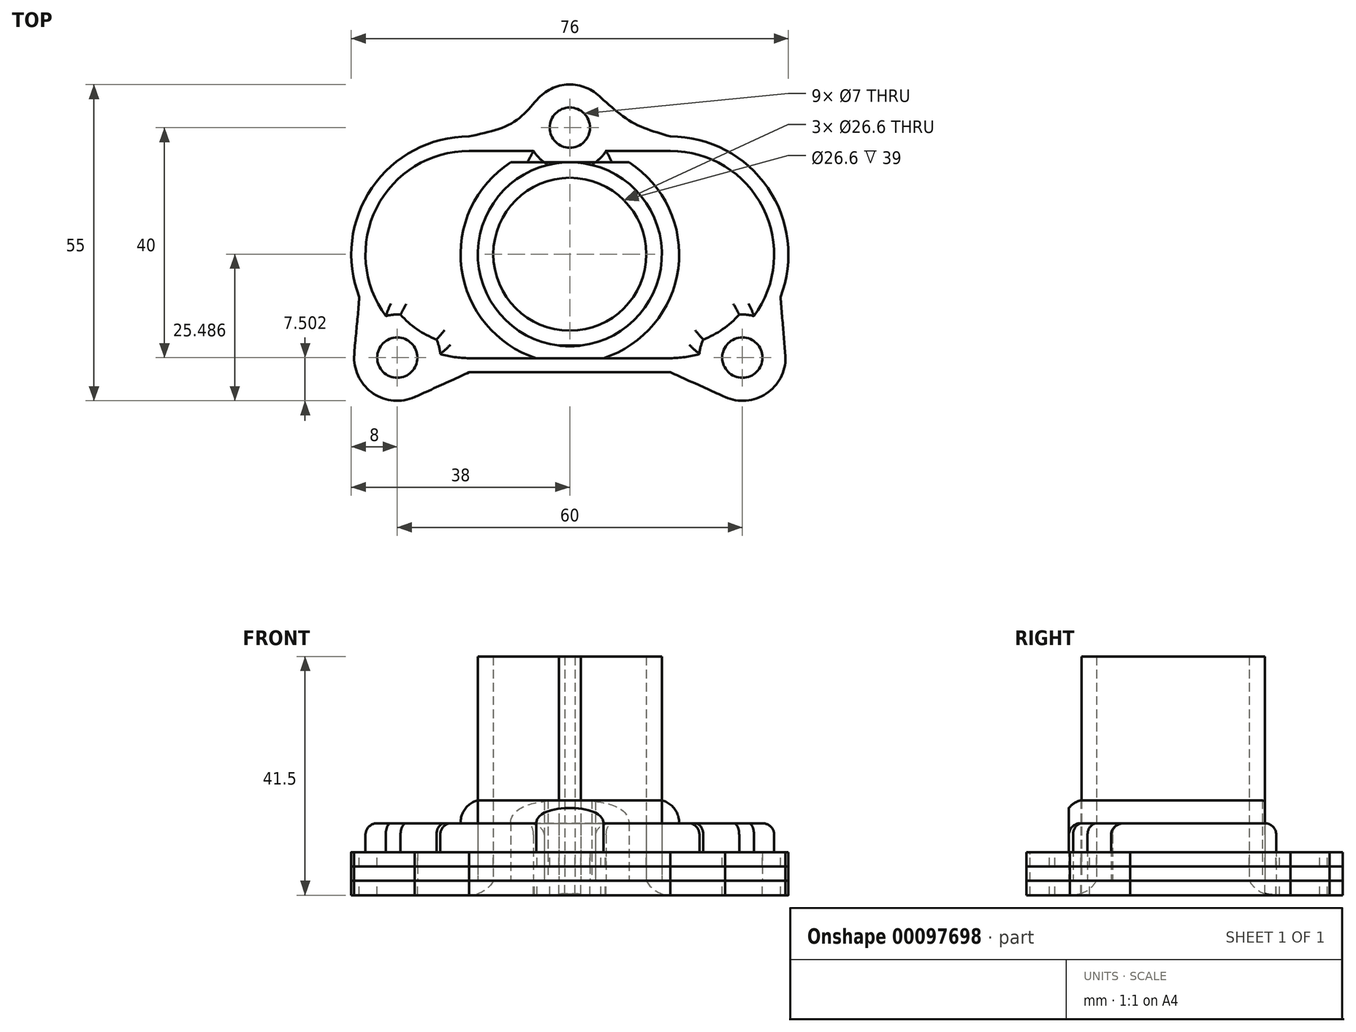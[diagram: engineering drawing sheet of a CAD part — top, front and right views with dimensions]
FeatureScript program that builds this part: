
annotation { "Feature Type Name" : "Feature", "Feature Type Description" : "" }
export const myFeature = defineFeature(function(context is Context, id is Id, definition is map)
    precondition{}
    {
        {
            var Q0;
            Q0=qCreatedBy(makeId("Top.planeOp"),FACE);
            var sketch = newSketch(context, id + "F0", { "sketchPlane" : qUnion([Q0])});
            skCircle(sketch, "E0", {"center": v(0, 24.43) * mm, "radius": 3.5 * mm});
            skCircle(sketch, "E1", {"center": v(30, -15.57) * mm, "radius": 3.5 * mm});
            skCircle(sketch, "E2", {"center": v(-30, -15.57) * mm, "radius": 3.5 * mm});
            skCircle(sketch, "E3", {"center": v(0, 24.43) * mm, "radius": 7.5 * mm});
            skCircle(sketch, "E4", {"center": v(30, -15.57) * mm, "radius": 7.5 * mm});
            skCircle(sketch, "E5", {"center": v(-30, -15.57) * mm, "radius": 7.5 * mm});
            skLineSegment(sketch, "E6", {"start": v(7.34, 22.9) * mm, "end": v(17.5, 22.9) * mm});
            skLineSegment(sketch, "E7", {"start": v(-17.5, -18.1) * mm, "end": v(17.5, -18.1) * mm});
            skLineSegment(sketch, "E8", {"start": v(-7.7, 22.9) * mm, "end": v(-17.5, 22.9) * mm});
            skLineSegment(sketch, "E9", {"start": v(-17.5, 15.9) * mm, "end": v(17.5, 15.9) * mm});
            skLineSegment(sketch, "E10", {"start": v(-17.5, -11.1) * mm, "end": v(17.5, -11.1) * mm});
            skArc(sketch, "E11", {"start": v(17.5, -11.1) * mm, "mid": v(31, 2.4) * mm, "end": v(17.5, 15.9) * mm});
            skArc(sketch, "E12", {"start": v(-17.5, 15.9) * mm, "mid": v(-31, 2.4) * mm, "end": v(-17.5, -11.1) * mm});
            skFitSpline(sketch, "E13", {"points": [v(-17.5, 22.9) * mm, v(-10.03, 25.23) * mm, v(-5.72, 29.28) * mm], "startDerivative": vector(15.12, 3.6) * mm, "endDerivative": vector(8.27, 9.34) * mm});
            skFitSpline(sketch, "E14", {"points": [v(17.5, 22.9) * mm, v(11.1, 25.23) * mm, v(5.4, 29.63) * mm], "startDerivative": vector(-13.33, 4.18) * mm, "endDerivative": vector(-10.87, 9.3) * mm});
            skArc(sketch, "E15", {"start": v(17.5, -18.1) * mm, "mid": v(38, 2.4) * mm, "end": v(17.5, 22.9) * mm});
            skArc(sketch, "E16", {"start": v(-17.5, 22.9) * mm, "mid": v(-38, 2.4) * mm, "end": v(-17.5, -18.1) * mm});
            skFitSpline(sketch, "E17", {"points": [v(27, -22.44) * mm, v(17.5, -18.1) * mm], "startDerivative": vector(-8.6, 4.02) * mm, "endDerivative": vector(-8.6, 4.02) * mm});
            skFitSpline(sketch, "E18", {"points": [v(-17.5, -18.1) * mm, v(-27, -22.44) * mm], "startDerivative": vector(-8, -3.6) * mm, "endDerivative": vector(-8, -3.6) * mm});
            skFitSpline(sketch, "E19", {"points": [v(36.62, -5) * mm, v(37.5, -15.5) * mm], "startDerivative": vector(0.87, -10.65) * mm, "endDerivative": vector(0.87, -10.65) * mm});
            skFitSpline(sketch, "E20", {"points": [v(-37.5, -15.5) * mm, v(-36.62, -5) * mm], "startDerivative": vector(0.62, 11.41) * mm, "endDerivative": vector(0.62, 11.41) * mm});
            skLineSegment(sketch, "E21", {"start": v(-17.5, 20.4) * mm, "end": v(17.5, 20.4) * mm});
            skLineSegment(sketch, "E22", {"start": v(-17.5, -15.66) * mm, "end": v(17.5, -15.66) * mm});
            skArc(sketch, "E23", {"start": v(17.5, -15.66) * mm, "mid": v(35.53, 2.36) * mm, "end": v(17.5, 20.4) * mm});
            skArc(sketch, "E24", {"start": v(-17.5, 20.4) * mm, "mid": v(-35.53, 2.36) * mm, "end": v(-17.5, -15.66) * mm});
            skLineSegment(sketch, "E25", {"start": v(-17.5, 18.4) * mm, "end": v(17.5, 18.4) * mm});
            skLineSegment(sketch, "E26", {"start": v(-17.5, -13.47) * mm, "end": v(17.5, -13.47) * mm});
            skArc(sketch, "E27", {"start": v(17.5, -13.47) * mm, "mid": v(33.43, 2.46) * mm, "end": v(17.5, 18.4) * mm});
            skArc(sketch, "E28", {"start": v(-17.5, 18.4) * mm, "mid": v(-33.43, 2.46) * mm, "end": v(-17.5, -13.47) * mm});
            skCircle(sketch, "E29", {"center": v(0, 2.42) * mm, "radius": 16 * mm});
            skCircle(sketch, "E30", {"center": v(0, 2.42) * mm, "radius": 13.3 * mm});
            skCircle(sketch, "E31", {"center": v(0, 2.42) * mm, "radius": 19 * mm});
            skSolve(sketch);
        }
        {
            var Q0;
            {var subQ1=sQuery(id+"F0.wireOp",EDGE,"E13");Q0=makeQuery(id+"F0.imprint","IMPRINT",FACE,{"disambiguationData":[TD([[makeQuery(id+"F0.imprint","IMPRINT",EDGE,{"derivedFrom":subQ1}),-1.0]])]});}
            var Q1;
            {var subQ0=sQuery(id+"F0.wireOp",EDGE,"E16");var subQ1=sQuery(id+"F0.wireOp",EDGE,"E2");var subQ2=makeQuery(id+"F0.imprint","INTERSECT",VERTEX,{"disambiguationData":[OD(0.0)],"derivedFrom":[subQ1,subQ0]});Q1=makeQuery(id+"F0.imprint","IMPRINT",FACE,{"disambiguationData":[TD([[makeQuery(id+"F0.imprint","IMPRINT",EDGE,{"disambiguationData":[TD([[subQ2,1.0]])],"derivedFrom":subQ1}),-1.0]])]});}
            var Q2;
            {var subQ6=sQuery(id+"F0.wireOp",EDGE,"E7");Q2=makeQuery(id+"F0.imprint","IMPRINT",FACE,{"disambiguationData":[TD([[makeQuery(id+"F0.imprint","IMPRINT",EDGE,{"derivedFrom":subQ6}),1.0]])]});}
            var Q3;
            {var subQ0=sQuery(id+"F0.wireOp",EDGE,"E18");var subQ1=sQuery(id+"F0.wireOp",EDGE,"E5");var subQ2=makeQuery(id+"F0.imprint","INTERSECT",VERTEX,{"disambiguationData":[OD(1.0)],"derivedFrom":[subQ1,subQ0]});Q3=makeQuery(id+"F0.imprint","IMPRINT",FACE,{"disambiguationData":[TD([[makeQuery(id+"F0.imprint","IMPRINT",EDGE,{"disambiguationData":[TD([[subQ2,-1.0]])],"derivedFrom":subQ1}),-1.0]])]});}
            var Q4;
            {var subQ6=sQuery(id+"F0.wireOp",EDGE,"E16");var subQ10=sQuery(id+"F0.wireOp",EDGE,"E2");var subQ11=makeQuery(id+"F0.imprint","INTERSECT",VERTEX,{"disambiguationData":[OD(0.0)],"derivedFrom":[subQ10,subQ6]});Q4=makeQuery(id+"F0.imprint","IMPRINT",FACE,{"disambiguationData":[TD([[makeQuery(id+"F0.imprint","IMPRINT",EDGE,{"disambiguationData":[TD([[subQ11,-1.0]])],"derivedFrom":subQ10}),-1.0]])]});}
            var Q5;
            {var subQ0=sQuery(id+"F0.wireOp",EDGE,"E20");var subQ1=sQuery(id+"F0.wireOp",EDGE,"E5");var subQ2=makeQuery(id+"F0.imprint","INTERSECT",VERTEX,{"disambiguationData":[OD(1.0)],"derivedFrom":[subQ1,subQ0]});Q5=makeQuery(id+"F0.imprint","IMPRINT",FACE,{"disambiguationData":[TD([[makeQuery(id+"F0.imprint","IMPRINT",EDGE,{"disambiguationData":[TD([[subQ2,1.0]])],"derivedFrom":subQ1}),-1.0]])]});}
            var Q6;
            {var subQ0=sQuery(id+"F0.wireOp",EDGE,"E6");Q6=makeQuery(id+"F0.imprint","IMPRINT",FACE,{"disambiguationData":[TD([[makeQuery(id+"F0.imprint","IMPRINT",EDGE,{"derivedFrom":subQ0}),1.0]])]});}
            var Q7;
            {var subQ0=sQuery(id+"F0.wireOp",EDGE,"E6");Q7=makeQuery(id+"F0.imprint","IMPRINT",FACE,{"disambiguationData":[TD([[makeQuery(id+"F0.imprint","IMPRINT",EDGE,{"derivedFrom":subQ0}),-1.0]])]});}
            var Q8;
            {var subQ0=sQuery(id+"F0.wireOp",EDGE,"E19");var subQ1=sQuery(id+"F0.wireOp",EDGE,"E4");var subQ2=makeQuery(id+"F0.imprint","INTERSECT",VERTEX,{"disambiguationData":[OD(1.0)],"derivedFrom":[subQ1,subQ0]});Q8=makeQuery(id+"F0.imprint","IMPRINT",FACE,{"disambiguationData":[TD([[makeQuery(id+"F0.imprint","IMPRINT",EDGE,{"disambiguationData":[TD([[subQ2,-1.0]])],"derivedFrom":subQ1}),-1.0]])]});}
            var Q9;
            {var subQ6=sQuery(id+"F0.wireOp",EDGE,"E15");var subQ10=sQuery(id+"F0.wireOp",EDGE,"E1");var subQ12=makeQuery(id+"F0.imprint","INTERSECT",VERTEX,{"disambiguationData":[OD(0.0)],"derivedFrom":[subQ10,subQ6]});Q9=makeQuery(id+"F0.imprint","IMPRINT",FACE,{"disambiguationData":[TD([[makeQuery(id+"F0.imprint","IMPRINT",EDGE,{"disambiguationData":[TD([[subQ12,-1.0]])],"derivedFrom":subQ10}),-1.0]])]});}
            var Q10;
            {var subQ0=sQuery(id+"F0.wireOp",EDGE,"E17");var subQ1=sQuery(id+"F0.wireOp",EDGE,"E4");var subQ2=makeQuery(id+"F0.imprint","INTERSECT",VERTEX,{"disambiguationData":[OD(1.0)],"derivedFrom":[subQ1,subQ0]});Q10=makeQuery(id+"F0.imprint","IMPRINT",FACE,{"disambiguationData":[TD([[makeQuery(id+"F0.imprint","IMPRINT",EDGE,{"disambiguationData":[TD([[subQ2,1.0]])],"derivedFrom":subQ1}),-1.0]])]});}
            var Q11;
            {var subQ0=sQuery(id+"F0.wireOp",EDGE,"E15");var subQ5=sQuery(id+"F0.wireOp",EDGE,"E1");var subQ6=makeQuery(id+"F0.imprint","INTERSECT",VERTEX,{"disambiguationData":[OD(0.0)],"derivedFrom":[subQ5,subQ0]});Q11=makeQuery(id+"F0.imprint","IMPRINT",FACE,{"disambiguationData":[TD([[makeQuery(id+"F0.imprint","IMPRINT",EDGE,{"disambiguationData":[TD([[subQ6,1.0]])],"derivedFrom":subQ5}),-1.0]])]});}
            var Q12;
            {var subQ0=sQuery(id+"F0.wireOp",EDGE,"E25");var subQ1=sQuery(id+"F0.wireOp",EDGE,"E3");var subQ2=makeQuery(id+"F0.imprint","INTERSECT",VERTEX,{"disambiguationData":[OD(0.0)],"derivedFrom":[subQ1,subQ0]});Q12=makeQuery(id+"F0.imprint","IMPRINT",FACE,{"disambiguationData":[TD([[makeQuery(id+"F0.imprint","IMPRINT",EDGE,{"disambiguationData":[TD([[subQ2,-1.0]])],"derivedFrom":subQ1}),1.0]])]});}
            var Q13;
            {var subQ0=sQuery(id+"F0.wireOp",EDGE,"E28");var subQ1=sQuery(id+"F0.wireOp",EDGE,"E5");var subQ2=makeQuery(id+"F0.imprint","INTERSECT",VERTEX,{"disambiguationData":[OD(0.0)],"derivedFrom":[subQ1,subQ0]});Q13=makeQuery(id+"F0.imprint","IMPRINT",FACE,{"disambiguationData":[TD([[makeQuery(id+"F0.imprint","IMPRINT",EDGE,{"disambiguationData":[TD([[subQ2,-1.0]])],"derivedFrom":subQ1}),1.0]])]});}
            var Q14;
            {var subQ0=sQuery(id+"F0.wireOp",EDGE,"E27");var subQ1=sQuery(id+"F0.wireOp",EDGE,"E4");var subQ2=makeQuery(id+"F0.imprint","INTERSECT",VERTEX,{"disambiguationData":[OD(0.0)],"derivedFrom":[subQ1,subQ0]});Q14=makeQuery(id+"F0.imprint","IMPRINT",FACE,{"disambiguationData":[TD([[makeQuery(id+"F0.imprint","IMPRINT",EDGE,{"disambiguationData":[TD([[subQ2,-1.0]])],"derivedFrom":subQ1}),1.0]])]});}
            var Q15;
            {var subQ0=sQuery(id+"F0.wireOp",EDGE,"E21");var subQ1=sQuery(id+"F0.wireOp",EDGE,"E3");var subQ2=makeQuery(id+"F0.imprint","INTERSECT",VERTEX,{"disambiguationData":[OD(0.0)],"derivedFrom":[subQ1,subQ0]});Q15=makeQuery(id+"F0.imprint","IMPRINT",FACE,{"disambiguationData":[TD([[makeQuery(id+"F0.imprint","IMPRINT",EDGE,{"disambiguationData":[TD([[subQ2,-1.0]])],"derivedFrom":subQ1}),1.0]])]});}
            var Q16;
            {var subQ0=sQuery(id+"F0.wireOp",EDGE,"E12");Q16=makeQuery(id+"F0.imprint","IMPRINT",FACE,{"disambiguationData":[TD([[makeQuery(id+"F0.imprint","IMPRINT",EDGE,{"derivedFrom":subQ0}),-1.0]])]});}
            var Q17;
            {var subQ0=sQuery(id+"F0.wireOp",EDGE,"E11");Q17=makeQuery(id+"F0.imprint","IMPRINT",FACE,{"disambiguationData":[TD([[makeQuery(id+"F0.imprint","IMPRINT",EDGE,{"derivedFrom":subQ0}),-1.0]])]});}
            var Q18;
            {var subQ0=sQuery(id+"F0.wireOp",EDGE,"E29");var subQ1=sQuery(id+"F0.wireOp",EDGE,"E3");var subQ2=makeQuery(id+"F0.imprint","INTERSECT",VERTEX,{"disambiguationData":[OD(0.0)],"derivedFrom":[subQ1,subQ0]});Q18=makeQuery(id+"F0.imprint","IMPRINT",FACE,{"disambiguationData":[TD([[makeQuery(id+"F0.imprint","IMPRINT",EDGE,{"disambiguationData":[TD([[subQ2,-1.0]])],"derivedFrom":subQ1}),-1.0]])]});}
            var Q19;
            {var subQ0=sQuery(id+"F0.wireOp",EDGE,"E29");var subQ1=sQuery(id+"F0.wireOp",EDGE,"E3");var subQ2=makeQuery(id+"F0.imprint","INTERSECT",VERTEX,{"disambiguationData":[OD(0.0)],"derivedFrom":[subQ1,subQ0]});Q19=makeQuery(id+"F0.imprint","IMPRINT",FACE,{"disambiguationData":[TD([[makeQuery(id+"F0.imprint","IMPRINT",EDGE,{"disambiguationData":[TD([[subQ2,-1.0]])],"derivedFrom":subQ1}),1.0]])]});}
            var Q20;
            {var subQ0=sQuery(id+"F0.wireOp",EDGE,"E29");var subQ1=sQuery(id+"F0.wireOp",EDGE,"E3");var subQ2=makeQuery(id+"F0.imprint","INTERSECT",VERTEX,{"disambiguationData":[OD(1.0)],"derivedFrom":[subQ1,subQ0]});Q20=makeQuery(id+"F0.imprint","IMPRINT",FACE,{"disambiguationData":[TD([[makeQuery(id+"F0.imprint","IMPRINT",EDGE,{"disambiguationData":[TD([[subQ2,-1.0]])],"derivedFrom":subQ1}),1.0]])]});}
            var Q21;
            {var subQ0=sQuery(id+"F0.wireOp",EDGE,"E11");Q21=makeQuery(id+"F0.imprint","IMPRINT",FACE,{"disambiguationData":[TD([[makeQuery(id+"F0.imprint","IMPRINT",EDGE,{"derivedFrom":subQ0}),1.0]])]});}
            var Q22;
            {var subQ0=sQuery(id+"F0.wireOp",EDGE,"E12");Q22=makeQuery(id+"F0.imprint","IMPRINT",FACE,{"disambiguationData":[TD([[makeQuery(id+"F0.imprint","IMPRINT",EDGE,{"derivedFrom":subQ0}),1.0]])]});}
            var Q23;
            Q23=makeQuery(id+"F0.imprint","IMPRINT",FACE,{"disambiguationData":[TD([[makeQuery(id+"F0.imprint","IMPRINT",EDGE,{"derivedFrom":sQuery(id+"F0.wireOp",EDGE,"E30")}),-1.0]])]});
            var Q24;
            {var subQ0=sQuery(id+"F0.wireOp",EDGE,"E29");var subQ1=sQuery(id+"F0.wireOp",EDGE,"E10");var subQ2=makeQuery(id+"F0.imprint","INTERSECT",VERTEX,{"disambiguationData":[OD(0.0)],"derivedFrom":[subQ1,subQ0]});Q24=makeQuery(id+"F0.imprint","IMPRINT",FACE,{"disambiguationData":[TD([[makeQuery(id+"F0.imprint","IMPRINT",EDGE,{"disambiguationData":[TD([[subQ2,-1.0]])],"derivedFrom":subQ1}),-1.0]])]});}
            var Q25;
            {var subQ0=sQuery(id+"F0.wireOp",EDGE,"E31");var subQ1=sQuery(id+"F0.wireOp",EDGE,"E22");var subQ2=makeQuery(id+"F0.imprint","INTERSECT",VERTEX,{"disambiguationData":[OD(0.0)],"derivedFrom":[subQ1,subQ0]});Q25=makeQuery(id+"F0.imprint","IMPRINT",FACE,{"disambiguationData":[TD([[makeQuery(id+"F0.imprint","IMPRINT",EDGE,{"disambiguationData":[TD([[subQ2,-1.0]])],"derivedFrom":subQ1}),-1.0]])]});}
            var Q26;
            {var subQ0=sQuery(id+"F0.wireOp",EDGE,"E29");var subQ1=sQuery(id+"F0.wireOp",EDGE,"E9");var subQ2=makeQuery(id+"F0.imprint","INTERSECT",VERTEX,{"disambiguationData":[OD(1.0)],"derivedFrom":[subQ1,subQ0]});Q26=makeQuery(id+"F0.imprint","IMPRINT",FACE,{"disambiguationData":[TD([[makeQuery(id+"F0.imprint","IMPRINT",EDGE,{"disambiguationData":[TD([[subQ2,-1.0]])],"derivedFrom":subQ1}),-1.0]])]});}
            var Q27;
            {var subQ0=sQuery(id+"F0.wireOp",EDGE,"E31");var subQ1=sQuery(id+"F0.wireOp",EDGE,"E9");var subQ2=makeQuery(id+"F0.imprint","INTERSECT",VERTEX,{"disambiguationData":[OD(0.0)],"derivedFrom":[subQ1,subQ0]});Q27=makeQuery(id+"F0.imprint","IMPRINT",FACE,{"disambiguationData":[TD([[makeQuery(id+"F0.imprint","IMPRINT",EDGE,{"disambiguationData":[TD([[subQ2,-1.0]])],"derivedFrom":subQ1}),-1.0]])]});}
            var Q28;
            {var subQ0=sQuery(id+"F0.wireOp",EDGE,"E31");var subQ1=sQuery(id+"F0.wireOp",EDGE,"E10");var subQ2=makeQuery(id+"F0.imprint","INTERSECT",VERTEX,{"disambiguationData":[OD(0.0)],"derivedFrom":[subQ1,subQ0]});Q28=makeQuery(id+"F0.imprint","IMPRINT",FACE,{"disambiguationData":[TD([[makeQuery(id+"F0.imprint","IMPRINT",EDGE,{"disambiguationData":[TD([[subQ2,-1.0]])],"derivedFrom":subQ1}),-1.0]])]});}
            var Q29;
            {var subQ0=sQuery(id+"F0.wireOp",EDGE,"E29");var subQ1=sQuery(id+"F0.wireOp",EDGE,"E10");var subQ2=makeQuery(id+"F0.imprint","INTERSECT",VERTEX,{"disambiguationData":[OD(1.0)],"derivedFrom":[subQ1,subQ0]});Q29=makeQuery(id+"F0.imprint","IMPRINT",FACE,{"disambiguationData":[TD([[makeQuery(id+"F0.imprint","IMPRINT",EDGE,{"disambiguationData":[TD([[subQ2,-1.0]])],"derivedFrom":subQ1}),-1.0]])]});}
            var Q30;
            {var subQ1=sQuery(id+"F0.wireOp",EDGE,"E3");var subQ7=sQuery(id+"F0.wireOp",EDGE,"E25");var subQ8=makeQuery(id+"F0.imprint","INTERSECT",VERTEX,{"disambiguationData":[OD(0.0)],"derivedFrom":[subQ1,subQ7]});Q30=makeQuery(id+"F0.imprint","IMPRINT",FACE,{"disambiguationData":[TD([[makeQuery(id+"F0.imprint","IMPRINT",EDGE,{"disambiguationData":[TD([[subQ8,-1.0]])],"derivedFrom":subQ1}),-1.0]])]});}
            var Q31;
            {var subQ1=sQuery(id+"F0.wireOp",EDGE,"E3");var subQ5=sQuery(id+"F0.wireOp",EDGE,"E29");var subQ6=makeQuery(id+"F0.imprint","INTERSECT",VERTEX,{"disambiguationData":[OD(1.0)],"derivedFrom":[subQ1,subQ5]});Q31=makeQuery(id+"F0.imprint","IMPRINT",FACE,{"disambiguationData":[TD([[makeQuery(id+"F0.imprint","IMPRINT",EDGE,{"disambiguationData":[TD([[subQ6,-1.0]])],"derivedFrom":subQ1}),-1.0]])]});}
            var Q32;
            {var subQ7=sQuery(id+"F0.wireOp",EDGE,"E31");var subQ8=sQuery(id+"F0.wireOp",EDGE,"E0");var subQ9=makeQuery(id+"F0.imprint","INTERSECT",VERTEX,{"disambiguationData":[OD(0.0)],"derivedFrom":[subQ8,subQ7]});Q32=makeQuery(id+"F0.imprint","IMPRINT",FACE,{"disambiguationData":[TD([[makeQuery(id+"F0.imprint","IMPRINT",EDGE,{"disambiguationData":[TD([[subQ9,-1.0]])],"derivedFrom":subQ8}),-1.0]])]});}
            var Q33;
            {var subQ0=sQuery(id+"F0.wireOp",EDGE,"E31");var subQ1=sQuery(id+"F0.wireOp",EDGE,"E0");var subQ2=makeQuery(id+"F0.imprint","INTERSECT",VERTEX,{"disambiguationData":[OD(0.0)],"derivedFrom":[subQ1,subQ0]});Q33=makeQuery(id+"F0.imprint","IMPRINT",FACE,{"disambiguationData":[TD([[makeQuery(id+"F0.imprint","IMPRINT",EDGE,{"disambiguationData":[TD([[subQ2,1.0]])],"derivedFrom":subQ1}),-1.0]])]});}
            var Q34;
            {var subQ0=sQuery(id+"F0.wireOp",EDGE,"E29");var subQ1=sQuery(id+"F0.wireOp",EDGE,"E26");var subQ2=makeQuery(id+"F0.imprint","INTERSECT",VERTEX,{"disambiguationData":[OD(0.0)],"derivedFrom":[subQ1,subQ0]});Q34=makeQuery(id+"F0.imprint","IMPRINT",FACE,{"disambiguationData":[TD([[makeQuery(id+"F0.imprint","IMPRINT",EDGE,{"disambiguationData":[TD([[subQ2,-1.0]])],"derivedFrom":subQ1}),-1.0]])]});}
            var Q35;
            {var subQ3=sQuery(id+"F0.wireOp",EDGE,"E5");var subQ5=sQuery(id+"F0.wireOp",EDGE,"E28");var subQ11=makeQuery(id+"F0.imprint","INTERSECT",VERTEX,{"disambiguationData":[OD(0.0)],"derivedFrom":[subQ3,subQ5]});Q35=makeQuery(id+"F0.imprint","IMPRINT",FACE,{"disambiguationData":[TD([[makeQuery(id+"F0.imprint","IMPRINT",EDGE,{"disambiguationData":[TD([[subQ11,1.0]])],"derivedFrom":subQ3}),-1.0]])]});}
            var Q36;
            {var subQ4=sQuery(id+"F0.wireOp",EDGE,"E31");var subQ7=sQuery(id+"F0.wireOp",EDGE,"E22");var subQ9=makeQuery(id+"F0.imprint","INTERSECT",VERTEX,{"disambiguationData":[OD(0.0)],"derivedFrom":[subQ7,subQ4]});Q36=makeQuery(id+"F0.imprint","IMPRINT",FACE,{"disambiguationData":[TD([[makeQuery(id+"F0.imprint","IMPRINT",EDGE,{"disambiguationData":[TD([[subQ9,-1.0]])],"derivedFrom":subQ7}),1.0]])]});}
            var Q37;
            {var subQ0=sQuery(id+"F0.wireOp",EDGE,"E27");var subQ9=sQuery(id+"F0.wireOp",EDGE,"E4");var subQ11=makeQuery(id+"F0.imprint","INTERSECT",VERTEX,{"disambiguationData":[OD(1.0)],"derivedFrom":[subQ9,subQ0]});Q37=makeQuery(id+"F0.imprint","IMPRINT",FACE,{"disambiguationData":[TD([[makeQuery(id+"F0.imprint","IMPRINT",EDGE,{"disambiguationData":[TD([[subQ11,-1.0]])],"derivedFrom":subQ9}),-1.0]])]});}
            var Q38;
            {var subQ0=sQuery(id+"F0.wireOp",EDGE,"E23");var subQ1=sQuery(id+"F0.wireOp",EDGE,"E4");var subQ2=makeQuery(id+"F0.imprint","INTERSECT",VERTEX,{"disambiguationData":[OD(0.0)],"derivedFrom":[subQ1,subQ0]});Q38=makeQuery(id+"F0.imprint","IMPRINT",FACE,{"disambiguationData":[TD([[makeQuery(id+"F0.imprint","IMPRINT",EDGE,{"disambiguationData":[TD([[subQ2,-1.0]])],"derivedFrom":subQ1}),1.0]])]});}
            var Q39;
            {var subQ7=sQuery(id+"F0.wireOp",EDGE,"E3");var subQ9=sQuery(id+"F0.wireOp",EDGE,"E31");var subQ10=makeQuery(id+"F0.imprint","INTERSECT",VERTEX,{"disambiguationData":[OD(1.0)],"derivedFrom":[subQ7,subQ9]});Q39=makeQuery(id+"F0.imprint","IMPRINT",FACE,{"disambiguationData":[TD([[makeQuery(id+"F0.imprint","IMPRINT",EDGE,{"disambiguationData":[TD([[subQ10,-1.0]])],"derivedFrom":subQ7}),-1.0]])]});}
            var Q40;
            {var subQ0=sQuery(id+"F0.wireOp",EDGE,"E28");var subQ1=sQuery(id+"F0.wireOp",EDGE,"E5");var subQ2=makeQuery(id+"F0.imprint","INTERSECT",VERTEX,{"disambiguationData":[OD(0.0)],"derivedFrom":[subQ1,subQ0]});Q40=makeQuery(id+"F0.imprint","IMPRINT",FACE,{"disambiguationData":[TD([[makeQuery(id+"F0.imprint","IMPRINT",EDGE,{"disambiguationData":[TD([[subQ2,1.0]])],"derivedFrom":subQ1}),1.0]])]});}
            var Q41;
            {var subQ1=sQuery(id+"F0.wireOp",EDGE,"E21");var subQ5=sQuery(id+"F0.wireOp",EDGE,"E3");var subQ6=makeQuery(id+"F0.imprint","INTERSECT",VERTEX,{"disambiguationData":[OD(0.0)],"derivedFrom":[subQ5,subQ1]});Q41=makeQuery(id+"F0.imprint","IMPRINT",FACE,{"disambiguationData":[TD([[makeQuery(id+"F0.imprint","IMPRINT",EDGE,{"disambiguationData":[TD([[subQ6,-1.0]])],"derivedFrom":subQ5}),-1.0]])]});}
            var Q42;
            {var subQ0=sQuery(id+"F0.wireOp",EDGE,"E31");var subQ1=sQuery(id+"F0.wireOp",EDGE,"E3");var subQ2=makeQuery(id+"F0.imprint","INTERSECT",VERTEX,{"disambiguationData":[OD(0.0)],"derivedFrom":[subQ1,subQ0]});Q42=makeQuery(id+"F0.imprint","IMPRINT",FACE,{"disambiguationData":[TD([[makeQuery(id+"F0.imprint","IMPRINT",EDGE,{"disambiguationData":[TD([[subQ2,-1.0]])],"derivedFrom":subQ1}),-1.0]])]});}
            var Q43;
            {var subQ1=sQuery(id+"F0.wireOp",EDGE,"E3");var subQ6=sQuery(id+"F0.wireOp",EDGE,"E31");var subQ12=makeQuery(id+"F0.imprint","INTERSECT",VERTEX,{"disambiguationData":[OD(0.0)],"derivedFrom":[subQ1,subQ6]});Q43=makeQuery(id+"F0.imprint","IMPRINT",FACE,{"disambiguationData":[TD([[makeQuery(id+"F0.imprint","IMPRINT",EDGE,{"disambiguationData":[TD([[subQ12,-1.0]])],"derivedFrom":subQ1}),1.0]])]});}
            var Q44;
            {var subQ0=sQuery(id+"F0.wireOp",EDGE,"E25");var subQ1=sQuery(id+"F0.wireOp",EDGE,"E3");var subQ2=makeQuery(id+"F0.imprint","INTERSECT",VERTEX,{"disambiguationData":[OD(1.0)],"derivedFrom":[subQ1,subQ0]});Q44=makeQuery(id+"F0.imprint","IMPRINT",FACE,{"disambiguationData":[TD([[makeQuery(id+"F0.imprint","IMPRINT",EDGE,{"disambiguationData":[TD([[subQ2,-1.0]])],"derivedFrom":subQ1}),-1.0]])]});}
            var Q45;
            {var subQ0=sQuery(id+"F0.wireOp",EDGE,"E29");var subQ1=sQuery(id+"F0.wireOp",EDGE,"E25");var subQ2=makeQuery(id+"F0.imprint","INTERSECT",VERTEX,{"disambiguationData":[OD(0.0)],"derivedFrom":[subQ1,subQ0]});Q45=makeQuery(id+"F0.imprint","IMPRINT",FACE,{"disambiguationData":[TD([[makeQuery(id+"F0.imprint","IMPRINT",EDGE,{"disambiguationData":[TD([[subQ2,-1.0]])],"derivedFrom":subQ1}),1.0]])]});}
            extrude(context, id + "F1", {"entities" : qUnion([Q0, Q1, Q2, Q3, Q4, Q5, Q6, Q7, Q8, Q9, Q10, Q11, Q12, Q13, Q14, Q15, Q16, Q17, Q18, Q19, Q20, Q21, Q22, Q23, Q24, Q25, Q26, Q27, Q28, Q29, Q30, Q31, Q32, Q33, Q34, Q35, Q36, Q37, Q38, Q39, Q40, Q41, Q42, Q43, Q44, Q45]), "depth" : 5 * mm});
        }
        {
            var Q0;
            {var subQ0=sQuery(id+"F0.wireOp",EDGE,"E18");var subQ1=sQuery(id+"F0.wireOp",EDGE,"E5");var subQ2=makeQuery(id+"F0.imprint","INTERSECT",VERTEX,{"disambiguationData":[OD(1.0)],"derivedFrom":[subQ1,subQ0]});Q0=makeQuery(id+"F0.imprint","IMPRINT",FACE,{"disambiguationData":[TD([[makeQuery(id+"F0.imprint","IMPRINT",EDGE,{"disambiguationData":[TD([[subQ2,-1.0]])],"derivedFrom":subQ1}),-1.0]])]});}
            var Q1;
            {var subQ3=sQuery(id+"F0.wireOp",EDGE,"E16");var subQ5=sQuery(id+"F0.wireOp",EDGE,"E2");var subQ6=makeQuery(id+"F0.imprint","INTERSECT",VERTEX,{"disambiguationData":[OD(0.0)],"derivedFrom":[subQ5,subQ3]});Q1=makeQuery(id+"F0.imprint","IMPRINT",FACE,{"disambiguationData":[TD([[makeQuery(id+"F0.imprint","IMPRINT",EDGE,{"disambiguationData":[TD([[subQ6,-1.0]])],"derivedFrom":subQ5}),-1.0]])]});}
            var Q2;
            {var subQ0=sQuery(id+"F0.wireOp",EDGE,"E16");var subQ1=sQuery(id+"F0.wireOp",EDGE,"E2");var subQ2=makeQuery(id+"F0.imprint","INTERSECT",VERTEX,{"disambiguationData":[OD(0.0)],"derivedFrom":[subQ1,subQ0]});Q2=makeQuery(id+"F0.imprint","IMPRINT",FACE,{"disambiguationData":[TD([[makeQuery(id+"F0.imprint","IMPRINT",EDGE,{"disambiguationData":[TD([[subQ2,1.0]])],"derivedFrom":subQ1}),-1.0]])]});}
            var Q3;
            {var subQ1=sQuery(id+"F0.wireOp",EDGE,"E7");Q3=makeQuery(id+"F0.imprint","IMPRINT",FACE,{"disambiguationData":[TD([[makeQuery(id+"F0.imprint","IMPRINT",EDGE,{"derivedFrom":subQ1}),1.0]])]});}
            var Q4;
            {var subQ0=sQuery(id+"F0.wireOp",EDGE,"E25");var subQ1=sQuery(id+"F0.wireOp",EDGE,"E3");var subQ2=makeQuery(id+"F0.imprint","INTERSECT",VERTEX,{"disambiguationData":[OD(0.0)],"derivedFrom":[subQ1,subQ0]});Q4=makeQuery(id+"F0.imprint","IMPRINT",FACE,{"disambiguationData":[TD([[makeQuery(id+"F0.imprint","IMPRINT",EDGE,{"disambiguationData":[TD([[subQ2,-1.0]])],"derivedFrom":subQ1}),1.0]])]});}
            var Q5;
            {var subQ0=sQuery(id+"F0.wireOp",EDGE,"E28");var subQ1=sQuery(id+"F0.wireOp",EDGE,"E5");var subQ2=makeQuery(id+"F0.imprint","INTERSECT",VERTEX,{"disambiguationData":[OD(0.0)],"derivedFrom":[subQ1,subQ0]});Q5=makeQuery(id+"F0.imprint","IMPRINT",FACE,{"disambiguationData":[TD([[makeQuery(id+"F0.imprint","IMPRINT",EDGE,{"disambiguationData":[TD([[subQ2,-1.0]])],"derivedFrom":subQ1}),1.0]])]});}
            var Q6;
            Q6=makeQuery(id+"F0.imprint","IMPRINT",FACE,{"disambiguationData":[TD([[makeQuery(id+"F0.imprint","IMPRINT",EDGE,{"derivedFrom":sQuery(id+"F0.wireOp",EDGE,"E9")}),1.0]])]});
            var Q7;
            {var subQ0=sQuery(id+"F0.wireOp",EDGE,"E27");var subQ1=sQuery(id+"F0.wireOp",EDGE,"E4");var subQ2=makeQuery(id+"F0.imprint","INTERSECT",VERTEX,{"disambiguationData":[OD(0.0)],"derivedFrom":[subQ1,subQ0]});Q7=makeQuery(id+"F0.imprint","IMPRINT",FACE,{"disambiguationData":[TD([[makeQuery(id+"F0.imprint","IMPRINT",EDGE,{"disambiguationData":[TD([[subQ2,-1.0]])],"derivedFrom":subQ1}),1.0]])]});}
            var Q8;
            {var subQ0=sQuery(id+"F0.wireOp",EDGE,"E6");Q8=makeQuery(id+"F0.imprint","IMPRINT",FACE,{"disambiguationData":[TD([[makeQuery(id+"F0.imprint","IMPRINT",EDGE,{"derivedFrom":subQ0}),-1.0]])]});}
            var Q9;
            Q9=makeQuery(id+"F0.imprint","IMPRINT",FACE,{"disambiguationData":[TD([[makeQuery(id+"F0.imprint","IMPRINT",EDGE,{"derivedFrom":sQuery(id+"F0.wireOp",EDGE,"E0")}),-1.0]])]});
            var Q10;
            {var subQ0=sQuery(id+"F0.wireOp",EDGE,"E6");Q10=makeQuery(id+"F0.imprint","IMPRINT",FACE,{"disambiguationData":[TD([[makeQuery(id+"F0.imprint","IMPRINT",EDGE,{"derivedFrom":subQ0}),1.0]])]});}
            var Q11;
            {var subQ1=sQuery(id+"F0.wireOp",EDGE,"E13");Q11=makeQuery(id+"F0.imprint","IMPRINT",FACE,{"disambiguationData":[TD([[makeQuery(id+"F0.imprint","IMPRINT",EDGE,{"derivedFrom":subQ1}),-1.0]])]});}
            var Q12;
            {var subQ0=sQuery(id+"F0.wireOp",EDGE,"E15");var subQ1=sQuery(id+"F0.wireOp",EDGE,"E1");var subQ2=makeQuery(id+"F0.imprint","INTERSECT",VERTEX,{"disambiguationData":[OD(0.0)],"derivedFrom":[subQ1,subQ0]});Q12=makeQuery(id+"F0.imprint","IMPRINT",FACE,{"disambiguationData":[TD([[makeQuery(id+"F0.imprint","IMPRINT",EDGE,{"disambiguationData":[TD([[subQ2,1.0]])],"derivedFrom":subQ1}),-1.0]])]});}
            var Q13;
            {var subQ6=sQuery(id+"F0.wireOp",EDGE,"E15");var subQ10=sQuery(id+"F0.wireOp",EDGE,"E1");var subQ11=makeQuery(id+"F0.imprint","INTERSECT",VERTEX,{"disambiguationData":[OD(0.0)],"derivedFrom":[subQ10,subQ6]});Q13=makeQuery(id+"F0.imprint","IMPRINT",FACE,{"disambiguationData":[TD([[makeQuery(id+"F0.imprint","IMPRINT",EDGE,{"disambiguationData":[TD([[subQ11,-1.0]])],"derivedFrom":subQ10}),-1.0]])]});}
            var Q14;
            {var subQ0=sQuery(id+"F0.wireOp",EDGE,"E19");var subQ1=sQuery(id+"F0.wireOp",EDGE,"E4");var subQ2=makeQuery(id+"F0.imprint","INTERSECT",VERTEX,{"disambiguationData":[OD(1.0)],"derivedFrom":[subQ1,subQ0]});Q14=makeQuery(id+"F0.imprint","IMPRINT",FACE,{"disambiguationData":[TD([[makeQuery(id+"F0.imprint","IMPRINT",EDGE,{"disambiguationData":[TD([[subQ2,-1.0]])],"derivedFrom":subQ1}),-1.0]])]});}
            var Q15;
            {var subQ0=sQuery(id+"F0.wireOp",EDGE,"E17");var subQ1=sQuery(id+"F0.wireOp",EDGE,"E4");var subQ2=makeQuery(id+"F0.imprint","INTERSECT",VERTEX,{"disambiguationData":[OD(1.0)],"derivedFrom":[subQ1,subQ0]});Q15=makeQuery(id+"F0.imprint","IMPRINT",FACE,{"disambiguationData":[TD([[makeQuery(id+"F0.imprint","IMPRINT",EDGE,{"disambiguationData":[TD([[subQ2,1.0]])],"derivedFrom":subQ1}),-1.0]])]});}
            var Q16;
            {var subQ0=sQuery(id+"F0.wireOp",EDGE,"E20");var subQ1=sQuery(id+"F0.wireOp",EDGE,"E5");var subQ2=makeQuery(id+"F0.imprint","INTERSECT",VERTEX,{"disambiguationData":[OD(1.0)],"derivedFrom":[subQ1,subQ0]});Q16=makeQuery(id+"F0.imprint","IMPRINT",FACE,{"disambiguationData":[TD([[makeQuery(id+"F0.imprint","IMPRINT",EDGE,{"disambiguationData":[TD([[subQ2,1.0]])],"derivedFrom":subQ1}),-1.0]])]});}
            var Q17;
            {var subQ0=sQuery(id+"F0.wireOp",EDGE,"E29");var subQ1=sQuery(id+"F0.wireOp",EDGE,"E10");var subQ2=makeQuery(id+"F0.imprint","INTERSECT",VERTEX,{"disambiguationData":[OD(0.0)],"derivedFrom":[subQ1,subQ0]});Q17=makeQuery(id+"F0.imprint","IMPRINT",FACE,{"disambiguationData":[TD([[makeQuery(id+"F0.imprint","IMPRINT",EDGE,{"disambiguationData":[TD([[subQ2,-1.0]])],"derivedFrom":subQ1}),-1.0]])]});}
            var Q18;
            {var subQ15=sQuery(id+"F0.wireOp",EDGE,"E12");Q18=makeQuery(id+"F0.imprint","IMPRINT",FACE,{"disambiguationData":[TD([[makeQuery(id+"F0.imprint","IMPRINT",EDGE,{"derivedFrom":subQ15}),-1.0]])]});}
            var Q19;
            {var subQ0=sQuery(id+"F0.wireOp",EDGE,"E29");var subQ1=sQuery(id+"F0.wireOp",EDGE,"E3");var subQ2=makeQuery(id+"F0.imprint","INTERSECT",VERTEX,{"disambiguationData":[OD(0.0)],"derivedFrom":[subQ1,subQ0]});Q19=makeQuery(id+"F0.imprint","IMPRINT",FACE,{"disambiguationData":[TD([[makeQuery(id+"F0.imprint","IMPRINT",EDGE,{"disambiguationData":[TD([[subQ2,-1.0]])],"derivedFrom":subQ1}),1.0]])]});}
            var Q20;
            Q20=makeQuery(id+"F1.opExtrude","CAP_FACE",FACE,{"disambiguationData":[OSD([sQuery(id+"F0.wireOp",EDGE,"E0"),sQuery(id+"F0.wireOp",EDGE,"E1"),sQuery(id+"F0.wireOp",EDGE,"E2"),sQuery(id+"F0.wireOp",EDGE,"E3"),sQuery(id+"F0.wireOp",EDGE,"E4"),sQuery(id+"F0.wireOp",EDGE,"E5"),sQuery(id+"F0.wireOp",EDGE,"E7"),sQuery(id+"F0.wireOp",EDGE,"E13"),sQuery(id+"F0.wireOp",EDGE,"E14"),sQuery(id+"F0.wireOp",EDGE,"E15"),sQuery(id+"F0.wireOp",EDGE,"E16"),sQuery(id+"F0.wireOp",EDGE,"E17"),sQuery(id+"F0.wireOp",EDGE,"E18"),sQuery(id+"F0.wireOp",EDGE,"E19"),sQuery(id+"F0.wireOp",EDGE,"E20"),sQuery(id+"F0.wireOp",EDGE,"E25"),sQuery(id+"F0.wireOp",EDGE,"E26"),sQuery(id+"F0.wireOp",EDGE,"E27"),sQuery(id+"F0.wireOp",EDGE,"E28"),sQuery(id+"F0.wireOp",EDGE,"E29")])],"isStart":false});
            var Q21;
            {var subQ11=sQuery(id+"F0.wireOp",EDGE,"E11");Q21=makeQuery(id+"F0.imprint","IMPRINT",FACE,{"disambiguationData":[TD([[makeQuery(id+"F0.imprint","IMPRINT",EDGE,{"derivedFrom":subQ11}),-1.0]])]});}
            var Q22;
            {var subQ0=sQuery(id+"F0.wireOp",EDGE,"E12");Q22=makeQuery(id+"F0.imprint","IMPRINT",FACE,{"disambiguationData":[TD([[makeQuery(id+"F0.imprint","IMPRINT",EDGE,{"derivedFrom":subQ0}),1.0]])]});}
            var Q23;
            Q23=makeQuery(id+"F0.imprint","IMPRINT",FACE,{"disambiguationData":[TD([[makeQuery(id+"F0.imprint","IMPRINT",EDGE,{"derivedFrom":sQuery(id+"F0.wireOp",EDGE,"E30")}),-1.0]])]});
            var Q24;
            {var subQ0=sQuery(id+"F0.wireOp",EDGE,"E11");Q24=makeQuery(id+"F0.imprint","IMPRINT",FACE,{"disambiguationData":[TD([[makeQuery(id+"F0.imprint","IMPRINT",EDGE,{"derivedFrom":subQ0}),1.0]])]});}
            var Q25;
            {var subQ0=sQuery(id+"F0.wireOp",EDGE,"E31");var subQ1=sQuery(id+"F0.wireOp",EDGE,"E9");var subQ2=makeQuery(id+"F0.imprint","INTERSECT",VERTEX,{"disambiguationData":[OD(0.0)],"derivedFrom":[subQ1,subQ0]});Q25=makeQuery(id+"F0.imprint","IMPRINT",FACE,{"disambiguationData":[TD([[makeQuery(id+"F0.imprint","IMPRINT",EDGE,{"disambiguationData":[TD([[subQ2,-1.0]])],"derivedFrom":subQ1}),-1.0]])]});}
            var Q26;
            {var subQ1=sQuery(id+"F0.wireOp",EDGE,"E3");var subQ7=sQuery(id+"F0.wireOp",EDGE,"E25");var subQ8=makeQuery(id+"F0.imprint","INTERSECT",VERTEX,{"disambiguationData":[OD(0.0)],"derivedFrom":[subQ1,subQ7]});Q26=makeQuery(id+"F0.imprint","IMPRINT",FACE,{"disambiguationData":[TD([[makeQuery(id+"F0.imprint","IMPRINT",EDGE,{"disambiguationData":[TD([[subQ8,-1.0]])],"derivedFrom":subQ1}),-1.0]])]});}
            var Q27;
            {var subQ1=sQuery(id+"F0.wireOp",EDGE,"E3");var subQ5=sQuery(id+"F0.wireOp",EDGE,"E29");var subQ6=makeQuery(id+"F0.imprint","INTERSECT",VERTEX,{"disambiguationData":[OD(1.0)],"derivedFrom":[subQ1,subQ5]});Q27=makeQuery(id+"F0.imprint","IMPRINT",FACE,{"disambiguationData":[TD([[makeQuery(id+"F0.imprint","IMPRINT",EDGE,{"disambiguationData":[TD([[subQ6,-1.0]])],"derivedFrom":subQ1}),-1.0]])]});}
            var Q28;
            {var subQ0=sQuery(id+"F0.wireOp",EDGE,"E29");var subQ1=sQuery(id+"F0.wireOp",EDGE,"E9");var subQ2=makeQuery(id+"F0.imprint","INTERSECT",VERTEX,{"disambiguationData":[OD(1.0)],"derivedFrom":[subQ1,subQ0]});Q28=makeQuery(id+"F0.imprint","IMPRINT",FACE,{"disambiguationData":[TD([[makeQuery(id+"F0.imprint","IMPRINT",EDGE,{"disambiguationData":[TD([[subQ2,-1.0]])],"derivedFrom":subQ1}),-1.0]])]});}
            var Q29;
            {var subQ0=sQuery(id+"F0.wireOp",EDGE,"E29");var subQ1=sQuery(id+"F0.wireOp",EDGE,"E10");var subQ2=makeQuery(id+"F0.imprint","INTERSECT",VERTEX,{"disambiguationData":[OD(1.0)],"derivedFrom":[subQ1,subQ0]});Q29=makeQuery(id+"F0.imprint","IMPRINT",FACE,{"disambiguationData":[TD([[makeQuery(id+"F0.imprint","IMPRINT",EDGE,{"disambiguationData":[TD([[subQ2,-1.0]])],"derivedFrom":subQ1}),-1.0]])]});}
            var Q30;
            {var subQ0=sQuery(id+"F0.wireOp",EDGE,"E31");var subQ1=sQuery(id+"F0.wireOp",EDGE,"E10");var subQ2=makeQuery(id+"F0.imprint","INTERSECT",VERTEX,{"disambiguationData":[OD(0.0)],"derivedFrom":[subQ1,subQ0]});Q30=makeQuery(id+"F0.imprint","IMPRINT",FACE,{"disambiguationData":[TD([[makeQuery(id+"F0.imprint","IMPRINT",EDGE,{"disambiguationData":[TD([[subQ2,-1.0]])],"derivedFrom":subQ1}),-1.0]])]});}
            var Q31;
            {var subQ0=sQuery(id+"F0.wireOp",EDGE,"E31");var subQ1=sQuery(id+"F0.wireOp",EDGE,"E22");var subQ2=makeQuery(id+"F0.imprint","INTERSECT",VERTEX,{"disambiguationData":[OD(0.0)],"derivedFrom":[subQ1,subQ0]});Q31=makeQuery(id+"F0.imprint","IMPRINT",FACE,{"disambiguationData":[TD([[makeQuery(id+"F0.imprint","IMPRINT",EDGE,{"disambiguationData":[TD([[subQ2,-1.0]])],"derivedFrom":subQ1}),-1.0]])]});}
            var Q32;
            {var subQ0=sQuery(id+"F0.wireOp",EDGE,"E29");var subQ1=sQuery(id+"F0.wireOp",EDGE,"E3");var subQ2=makeQuery(id+"F0.imprint","INTERSECT",VERTEX,{"disambiguationData":[OD(1.0)],"derivedFrom":[subQ1,subQ0]});Q32=makeQuery(id+"F0.imprint","IMPRINT",FACE,{"disambiguationData":[TD([[makeQuery(id+"F0.imprint","IMPRINT",EDGE,{"disambiguationData":[TD([[subQ2,-1.0]])],"derivedFrom":subQ1}),1.0]])]});}
            var Q33;
            {var subQ7=sQuery(id+"F0.wireOp",EDGE,"E31");var subQ8=sQuery(id+"F0.wireOp",EDGE,"E0");var subQ9=makeQuery(id+"F0.imprint","INTERSECT",VERTEX,{"disambiguationData":[OD(0.0)],"derivedFrom":[subQ8,subQ7]});Q33=makeQuery(id+"F0.imprint","IMPRINT",FACE,{"disambiguationData":[TD([[makeQuery(id+"F0.imprint","IMPRINT",EDGE,{"disambiguationData":[TD([[subQ9,-1.0]])],"derivedFrom":subQ8}),-1.0]])]});}
            var Q34;
            {var subQ7=sQuery(id+"F0.wireOp",EDGE,"E3");var subQ9=sQuery(id+"F0.wireOp",EDGE,"E31");var subQ10=makeQuery(id+"F0.imprint","INTERSECT",VERTEX,{"disambiguationData":[OD(1.0)],"derivedFrom":[subQ7,subQ9]});Q34=makeQuery(id+"F0.imprint","IMPRINT",FACE,{"disambiguationData":[TD([[makeQuery(id+"F0.imprint","IMPRINT",EDGE,{"disambiguationData":[TD([[subQ10,-1.0]])],"derivedFrom":subQ7}),-1.0]])]});}
            var Q35;
            {var subQ0=sQuery(id+"F0.wireOp",EDGE,"E25");var subQ1=sQuery(id+"F0.wireOp",EDGE,"E3");var subQ2=makeQuery(id+"F0.imprint","INTERSECT",VERTEX,{"disambiguationData":[OD(1.0)],"derivedFrom":[subQ1,subQ0]});Q35=makeQuery(id+"F0.imprint","IMPRINT",FACE,{"disambiguationData":[TD([[makeQuery(id+"F0.imprint","IMPRINT",EDGE,{"disambiguationData":[TD([[subQ2,-1.0]])],"derivedFrom":subQ1}),-1.0]])]});}
            var Q36;
            {var subQ1=sQuery(id+"F0.wireOp",EDGE,"E3");var subQ6=sQuery(id+"F0.wireOp",EDGE,"E31");var subQ12=makeQuery(id+"F0.imprint","INTERSECT",VERTEX,{"disambiguationData":[OD(0.0)],"derivedFrom":[subQ1,subQ6]});Q36=makeQuery(id+"F0.imprint","IMPRINT",FACE,{"disambiguationData":[TD([[makeQuery(id+"F0.imprint","IMPRINT",EDGE,{"disambiguationData":[TD([[subQ12,-1.0]])],"derivedFrom":subQ1}),1.0]])]});}
            var Q37;
            {var subQ0=sQuery(id+"F0.wireOp",EDGE,"E31");var subQ1=sQuery(id+"F0.wireOp",EDGE,"E3");var subQ2=makeQuery(id+"F0.imprint","INTERSECT",VERTEX,{"disambiguationData":[OD(0.0)],"derivedFrom":[subQ1,subQ0]});Q37=makeQuery(id+"F0.imprint","IMPRINT",FACE,{"disambiguationData":[TD([[makeQuery(id+"F0.imprint","IMPRINT",EDGE,{"disambiguationData":[TD([[subQ2,-1.0]])],"derivedFrom":subQ1}),-1.0]])]});}
            var Q38;
            {var subQ1=sQuery(id+"F0.wireOp",EDGE,"E21");var subQ5=sQuery(id+"F0.wireOp",EDGE,"E3");var subQ6=makeQuery(id+"F0.imprint","INTERSECT",VERTEX,{"disambiguationData":[OD(0.0)],"derivedFrom":[subQ5,subQ1]});Q38=makeQuery(id+"F0.imprint","IMPRINT",FACE,{"disambiguationData":[TD([[makeQuery(id+"F0.imprint","IMPRINT",EDGE,{"disambiguationData":[TD([[subQ6,-1.0]])],"derivedFrom":subQ5}),-1.0]])]});}
            var Q39;
            {var subQ0=sQuery(id+"F0.wireOp",EDGE,"E23");var subQ1=sQuery(id+"F0.wireOp",EDGE,"E4");var subQ2=makeQuery(id+"F0.imprint","INTERSECT",VERTEX,{"disambiguationData":[OD(0.0)],"derivedFrom":[subQ1,subQ0]});Q39=makeQuery(id+"F0.imprint","IMPRINT",FACE,{"disambiguationData":[TD([[makeQuery(id+"F0.imprint","IMPRINT",EDGE,{"disambiguationData":[TD([[subQ2,-1.0]])],"derivedFrom":subQ1}),1.0]])]});}
            var Q40;
            {var subQ0=sQuery(id+"F0.wireOp",EDGE,"E27");var subQ9=sQuery(id+"F0.wireOp",EDGE,"E4");var subQ11=makeQuery(id+"F0.imprint","INTERSECT",VERTEX,{"disambiguationData":[OD(1.0)],"derivedFrom":[subQ9,subQ0]});Q40=makeQuery(id+"F0.imprint","IMPRINT",FACE,{"disambiguationData":[TD([[makeQuery(id+"F0.imprint","IMPRINT",EDGE,{"disambiguationData":[TD([[subQ11,-1.0]])],"derivedFrom":subQ9}),-1.0]])]});}
            var Q41;
            {var subQ4=sQuery(id+"F0.wireOp",EDGE,"E31");var subQ7=sQuery(id+"F0.wireOp",EDGE,"E22");var subQ9=makeQuery(id+"F0.imprint","INTERSECT",VERTEX,{"disambiguationData":[OD(0.0)],"derivedFrom":[subQ7,subQ4]});Q41=makeQuery(id+"F0.imprint","IMPRINT",FACE,{"disambiguationData":[TD([[makeQuery(id+"F0.imprint","IMPRINT",EDGE,{"disambiguationData":[TD([[subQ9,-1.0]])],"derivedFrom":subQ7}),1.0]])]});}
            var Q42;
            {var subQ3=sQuery(id+"F0.wireOp",EDGE,"E5");var subQ5=sQuery(id+"F0.wireOp",EDGE,"E28");var subQ11=makeQuery(id+"F0.imprint","INTERSECT",VERTEX,{"disambiguationData":[OD(0.0)],"derivedFrom":[subQ3,subQ5]});Q42=makeQuery(id+"F0.imprint","IMPRINT",FACE,{"disambiguationData":[TD([[makeQuery(id+"F0.imprint","IMPRINT",EDGE,{"disambiguationData":[TD([[subQ11,1.0]])],"derivedFrom":subQ3}),-1.0]])]});}
            var Q43;
            {var subQ0=sQuery(id+"F0.wireOp",EDGE,"E28");var subQ1=sQuery(id+"F0.wireOp",EDGE,"E5");var subQ2=makeQuery(id+"F0.imprint","INTERSECT",VERTEX,{"disambiguationData":[OD(0.0)],"derivedFrom":[subQ1,subQ0]});Q43=makeQuery(id+"F0.imprint","IMPRINT",FACE,{"disambiguationData":[TD([[makeQuery(id+"F0.imprint","IMPRINT",EDGE,{"disambiguationData":[TD([[subQ2,1.0]])],"derivedFrom":subQ1}),1.0]])]});}
            extrude(context, id + "F2", {"entities" : qUnion([Q0, Q1, Q2, Q3, Q4, Q5, Q6, Q7, Q8, Q9, Q10, Q11, Q12, Q13, Q14, Q15, Q16, Q17, Q18, Q19, Q20, Q21, Q22, Q23, Q24, Q25, Q26, Q27, Q28, Q29, Q30, Q31, Q32, Q33, Q34, Q35, Q36, Q37, Q38, Q39, Q40, Q41, Q42, Q43]), "oppositeDirection" : true, "depth" : 2.5 * mm});
        }
        {
            var Q0;
            {var subQ0=sQuery(id+"F0.wireOp",EDGE,"E12");Q0=makeQuery(id+"F0.imprint","IMPRINT",FACE,{"disambiguationData":[TD([[makeQuery(id+"F0.imprint","IMPRINT",EDGE,{"derivedFrom":subQ0}),1.0]])]});}
            var Q1;
            Q1=makeQuery(id+"F0.imprint","IMPRINT",FACE,{"disambiguationData":[TD([[makeQuery(id+"F0.imprint","IMPRINT",EDGE,{"derivedFrom":sQuery(id+"F0.wireOp",EDGE,"E30")}),-1.0]])]});
            var Q2;
            {var subQ0=sQuery(id+"F0.wireOp",EDGE,"E11");Q2=makeQuery(id+"F0.imprint","IMPRINT",FACE,{"disambiguationData":[TD([[makeQuery(id+"F0.imprint","IMPRINT",EDGE,{"derivedFrom":subQ0}),1.0]])]});}
            var Q3;
            {var subQ15=sQuery(id+"F0.wireOp",EDGE,"E12");Q3=makeQuery(id+"F0.imprint","IMPRINT",FACE,{"disambiguationData":[TD([[makeQuery(id+"F0.imprint","IMPRINT",EDGE,{"derivedFrom":subQ15}),-1.0]])]});}
            var Q4;
            {var subQ1=sQuery(id+"F0.wireOp",EDGE,"E21");var subQ5=sQuery(id+"F0.wireOp",EDGE,"E3");var subQ6=makeQuery(id+"F0.imprint","INTERSECT",VERTEX,{"disambiguationData":[OD(0.0)],"derivedFrom":[subQ5,subQ1]});Q4=makeQuery(id+"F0.imprint","IMPRINT",FACE,{"disambiguationData":[TD([[makeQuery(id+"F0.imprint","IMPRINT",EDGE,{"disambiguationData":[TD([[subQ6,-1.0]])],"derivedFrom":subQ5}),-1.0]])]});}
            var Q5;
            {var subQ1=sQuery(id+"F0.wireOp",EDGE,"E22");Q5=makeQuery(id+"F0.imprint","IMPRINT",FACE,{"disambiguationData":[TD([[makeQuery(id+"F0.imprint","IMPRINT",EDGE,{"derivedFrom":subQ1}),1.0]])]});}
            var Q6;
            {var subQ0=sQuery(id+"F0.wireOp",EDGE,"E28");var subQ1=sQuery(id+"F0.wireOp",EDGE,"E5");var subQ2=makeQuery(id+"F0.imprint","INTERSECT",VERTEX,{"disambiguationData":[OD(0.0)],"derivedFrom":[subQ1,subQ0]});Q6=makeQuery(id+"F0.imprint","IMPRINT",FACE,{"disambiguationData":[TD([[makeQuery(id+"F0.imprint","IMPRINT",EDGE,{"disambiguationData":[TD([[subQ2,-1.0]])],"derivedFrom":subQ1}),1.0]])]});}
            var Q7;
            {var subQ11=sQuery(id+"F0.wireOp",EDGE,"E11");Q7=makeQuery(id+"F0.imprint","IMPRINT",FACE,{"disambiguationData":[TD([[makeQuery(id+"F0.imprint","IMPRINT",EDGE,{"derivedFrom":subQ11}),-1.0]])]});}
            var Q8;
            {var subQ0=sQuery(id+"F0.wireOp",EDGE,"E29");var subQ1=sQuery(id+"F0.wireOp",EDGE,"E3");var subQ2=makeQuery(id+"F0.imprint","INTERSECT",VERTEX,{"disambiguationData":[OD(0.0)],"derivedFrom":[subQ1,subQ0]});Q8=makeQuery(id+"F0.imprint","IMPRINT",FACE,{"disambiguationData":[TD([[makeQuery(id+"F0.imprint","IMPRINT",EDGE,{"disambiguationData":[TD([[subQ2,-1.0]])],"derivedFrom":subQ1}),-1.0]])]});}
            var Q9;
            {var subQ0=sQuery(id+"F0.wireOp",EDGE,"E29");var subQ1=sQuery(id+"F0.wireOp",EDGE,"E3");var subQ2=makeQuery(id+"F0.imprint","INTERSECT",VERTEX,{"disambiguationData":[OD(0.0)],"derivedFrom":[subQ1,subQ0]});Q9=makeQuery(id+"F0.imprint","IMPRINT",FACE,{"disambiguationData":[TD([[makeQuery(id+"F0.imprint","IMPRINT",EDGE,{"disambiguationData":[TD([[subQ2,-1.0]])],"derivedFrom":subQ1}),1.0]])]});}
            var Q10;
            {var subQ5=sQuery(id+"F0.wireOp",EDGE,"E25");var subQ6=sQuery(id+"F0.wireOp",EDGE,"E3");var subQ7=makeQuery(id+"F0.imprint","INTERSECT",VERTEX,{"disambiguationData":[OD(1.0)],"derivedFrom":[subQ6,subQ5]});Q10=makeQuery(id+"F0.imprint","IMPRINT",FACE,{"disambiguationData":[TD([[makeQuery(id+"F0.imprint","IMPRINT",EDGE,{"disambiguationData":[TD([[subQ7,-1.0]])],"derivedFrom":subQ6}),-1.0]])]});}
            var Q11;
            {var subQ0=sQuery(id+"F0.wireOp",EDGE,"E27");var subQ1=sQuery(id+"F0.wireOp",EDGE,"E4");var subQ2=makeQuery(id+"F0.imprint","INTERSECT",VERTEX,{"disambiguationData":[OD(0.0)],"derivedFrom":[subQ1,subQ0]});Q11=makeQuery(id+"F0.imprint","IMPRINT",FACE,{"disambiguationData":[TD([[makeQuery(id+"F0.imprint","IMPRINT",EDGE,{"disambiguationData":[TD([[subQ2,-1.0]])],"derivedFrom":subQ1}),1.0]])]});}
            var Q12;
            {var subQ0=sQuery(id+"F0.wireOp",EDGE,"E29");var subQ1=sQuery(id+"F0.wireOp",EDGE,"E9");var subQ2=makeQuery(id+"F0.imprint","INTERSECT",VERTEX,{"disambiguationData":[OD(1.0)],"derivedFrom":[subQ1,subQ0]});Q12=makeQuery(id+"F0.imprint","IMPRINT",FACE,{"disambiguationData":[TD([[makeQuery(id+"F0.imprint","IMPRINT",EDGE,{"disambiguationData":[TD([[subQ2,-1.0]])],"derivedFrom":subQ1}),-1.0]])]});}
            var Q13;
            {var subQ1=sQuery(id+"F0.wireOp",EDGE,"E3");var subQ5=sQuery(id+"F0.wireOp",EDGE,"E29");var subQ6=makeQuery(id+"F0.imprint","INTERSECT",VERTEX,{"disambiguationData":[OD(1.0)],"derivedFrom":[subQ1,subQ5]});Q13=makeQuery(id+"F0.imprint","IMPRINT",FACE,{"disambiguationData":[TD([[makeQuery(id+"F0.imprint","IMPRINT",EDGE,{"disambiguationData":[TD([[subQ6,-1.0]])],"derivedFrom":subQ1}),-1.0]])]});}
            var Q14;
            {var subQ7=sQuery(id+"F0.wireOp",EDGE,"E3");var subQ9=sQuery(id+"F0.wireOp",EDGE,"E31");var subQ10=makeQuery(id+"F0.imprint","INTERSECT",VERTEX,{"disambiguationData":[OD(1.0)],"derivedFrom":[subQ7,subQ9]});Q14=makeQuery(id+"F0.imprint","IMPRINT",FACE,{"disambiguationData":[TD([[makeQuery(id+"F0.imprint","IMPRINT",EDGE,{"disambiguationData":[TD([[subQ10,-1.0]])],"derivedFrom":subQ7}),-1.0]])]});}
            var Q15;
            {var subQ0=sQuery(id+"F0.wireOp",EDGE,"E29");var subQ1=sQuery(id+"F0.wireOp",EDGE,"E10");var subQ2=makeQuery(id+"F0.imprint","INTERSECT",VERTEX,{"disambiguationData":[OD(1.0)],"derivedFrom":[subQ1,subQ0]});Q15=makeQuery(id+"F0.imprint","IMPRINT",FACE,{"disambiguationData":[TD([[makeQuery(id+"F0.imprint","IMPRINT",EDGE,{"disambiguationData":[TD([[subQ2,-1.0]])],"derivedFrom":subQ1}),-1.0]])]});}
            var Q16;
            {var subQ0=sQuery(id+"F0.wireOp",EDGE,"E31");var subQ1=sQuery(id+"F0.wireOp",EDGE,"E10");var subQ2=makeQuery(id+"F0.imprint","INTERSECT",VERTEX,{"disambiguationData":[OD(0.0)],"derivedFrom":[subQ1,subQ0]});Q16=makeQuery(id+"F0.imprint","IMPRINT",FACE,{"disambiguationData":[TD([[makeQuery(id+"F0.imprint","IMPRINT",EDGE,{"disambiguationData":[TD([[subQ2,-1.0]])],"derivedFrom":subQ1}),-1.0]])]});}
            var Q17;
            {var subQ0=sQuery(id+"F0.wireOp",EDGE,"E31");var subQ1=sQuery(id+"F0.wireOp",EDGE,"E9");var subQ2=makeQuery(id+"F0.imprint","INTERSECT",VERTEX,{"disambiguationData":[OD(0.0)],"derivedFrom":[subQ1,subQ0]});Q17=makeQuery(id+"F0.imprint","IMPRINT",FACE,{"disambiguationData":[TD([[makeQuery(id+"F0.imprint","IMPRINT",EDGE,{"disambiguationData":[TD([[subQ2,-1.0]])],"derivedFrom":subQ1}),-1.0]])]});}
            var Q18;
            {var subQ1=sQuery(id+"F0.wireOp",EDGE,"E3");var subQ7=sQuery(id+"F0.wireOp",EDGE,"E25");var subQ8=makeQuery(id+"F0.imprint","INTERSECT",VERTEX,{"disambiguationData":[OD(0.0)],"derivedFrom":[subQ1,subQ7]});Q18=makeQuery(id+"F0.imprint","IMPRINT",FACE,{"disambiguationData":[TD([[makeQuery(id+"F0.imprint","IMPRINT",EDGE,{"disambiguationData":[TD([[subQ8,-1.0]])],"derivedFrom":subQ1}),-1.0]])]});}
            var Q19;
            {var subQ0=sQuery(id+"F0.wireOp",EDGE,"E31");var subQ1=sQuery(id+"F0.wireOp",EDGE,"E3");var subQ2=makeQuery(id+"F0.imprint","INTERSECT",VERTEX,{"disambiguationData":[OD(0.0)],"derivedFrom":[subQ1,subQ0]});Q19=makeQuery(id+"F0.imprint","IMPRINT",FACE,{"disambiguationData":[TD([[makeQuery(id+"F0.imprint","IMPRINT",EDGE,{"disambiguationData":[TD([[subQ2,-1.0]])],"derivedFrom":subQ1}),-1.0]])]});}
            var Q20;
            {var subQ0=sQuery(id+"F0.wireOp",EDGE,"E29");var subQ1=sQuery(id+"F0.wireOp",EDGE,"E10");var subQ2=makeQuery(id+"F0.imprint","INTERSECT",VERTEX,{"disambiguationData":[OD(0.0)],"derivedFrom":[subQ1,subQ0]});Q20=makeQuery(id+"F0.imprint","IMPRINT",FACE,{"disambiguationData":[TD([[makeQuery(id+"F0.imprint","IMPRINT",EDGE,{"disambiguationData":[TD([[subQ2,-1.0]])],"derivedFrom":subQ1}),-1.0]])]});}
            var Q21;
            {var subQ0=sQuery(id+"F0.wireOp",EDGE,"E29");var subQ1=sQuery(id+"F0.wireOp",EDGE,"E3");var subQ2=makeQuery(id+"F0.imprint","INTERSECT",VERTEX,{"disambiguationData":[OD(1.0)],"derivedFrom":[subQ1,subQ0]});Q21=makeQuery(id+"F0.imprint","IMPRINT",FACE,{"disambiguationData":[TD([[makeQuery(id+"F0.imprint","IMPRINT",EDGE,{"disambiguationData":[TD([[subQ2,-1.0]])],"derivedFrom":subQ1}),1.0]])]});}
            var Q22;
            {var subQ0=sQuery(id+"F0.wireOp",EDGE,"E25");var subQ1=sQuery(id+"F0.wireOp",EDGE,"E3");var subQ2=makeQuery(id+"F0.imprint","INTERSECT",VERTEX,{"disambiguationData":[OD(0.0)],"derivedFrom":[subQ1,subQ0]});Q22=makeQuery(id+"F0.imprint","IMPRINT",FACE,{"disambiguationData":[TD([[makeQuery(id+"F0.imprint","IMPRINT",EDGE,{"disambiguationData":[TD([[subQ2,-1.0]])],"derivedFrom":subQ1}),1.0]])]});}
            var Q23;
            {var subQ0=sQuery(id+"F0.wireOp",EDGE,"E29");var subQ1=sQuery(id+"F0.wireOp",EDGE,"E26");var subQ2=makeQuery(id+"F0.imprint","INTERSECT",VERTEX,{"disambiguationData":[OD(0.0)],"derivedFrom":[subQ1,subQ0]});Q23=makeQuery(id+"F0.imprint","IMPRINT",FACE,{"disambiguationData":[TD([[makeQuery(id+"F0.imprint","IMPRINT",EDGE,{"disambiguationData":[TD([[subQ2,-1.0]])],"derivedFrom":subQ1}),-1.0]])]});}
            extrude(context, id + "F3", {"entities" : qUnion([Q0, Q1, Q2, Q3, Q4, Q5, Q6, Q7, Q8, Q9, Q10, Q11, Q12, Q13, Q14, Q15, Q16, Q17, Q18, Q19, Q20, Q21, Q22, Q23]), "depth" : 10 * mm});
        }
        {
            var Q0;
            Q0=makeQuery(id+"F0.imprint","IMPRINT",FACE,{"disambiguationData":[TD([[makeQuery(id+"F0.imprint","IMPRINT",EDGE,{"derivedFrom":sQuery(id+"F0.wireOp",EDGE,"E30")}),-1.0]])]});
            var Q1;
            {var subQ0=sQuery(id+"F0.wireOp",EDGE,"E29");var subQ1=sQuery(id+"F0.wireOp",EDGE,"E10");var subQ2=makeQuery(id+"F0.imprint","INTERSECT",VERTEX,{"disambiguationData":[OD(0.0)],"derivedFrom":[subQ1,subQ0]});Q1=makeQuery(id+"F0.imprint","IMPRINT",FACE,{"disambiguationData":[TD([[makeQuery(id+"F0.imprint","IMPRINT",EDGE,{"disambiguationData":[TD([[subQ2,-1.0]])],"derivedFrom":subQ1}),-1.0]])]});}
            var Q2;
            {var subQ0=sQuery(id+"F0.wireOp",EDGE,"E29");var subQ1=sQuery(id+"F0.wireOp",EDGE,"E3");var subQ2=makeQuery(id+"F0.imprint","INTERSECT",VERTEX,{"disambiguationData":[OD(0.0)],"derivedFrom":[subQ1,subQ0]});Q2=makeQuery(id+"F0.imprint","IMPRINT",FACE,{"disambiguationData":[TD([[makeQuery(id+"F0.imprint","IMPRINT",EDGE,{"disambiguationData":[TD([[subQ2,-1.0]])],"derivedFrom":subQ1}),-1.0]])]});}
            var Q3;
            {var subQ0=sQuery(id+"F0.wireOp",EDGE,"E29");var subQ1=sQuery(id+"F0.wireOp",EDGE,"E3");var subQ2=makeQuery(id+"F0.imprint","INTERSECT",VERTEX,{"disambiguationData":[OD(0.0)],"derivedFrom":[subQ1,subQ0]});Q3=makeQuery(id+"F0.imprint","IMPRINT",FACE,{"disambiguationData":[TD([[makeQuery(id+"F0.imprint","IMPRINT",EDGE,{"disambiguationData":[TD([[subQ2,-1.0]])],"derivedFrom":subQ1}),1.0]])]});}
            extrude(context, id + "F4", {"entities" : qUnion([Q0, Q1, Q2, Q3]), "depth" : 39 * mm});
        }
        {
            var Q0;
            {var subQ0=sQuery(id+"F0.wireOp",EDGE,"E24");Q0=makeQuery(id+"F3.opExtrude","CAP_EDGE",EDGE,{"disambiguationData":[OSD([subQ0]),TDD([makeQuery(id+"F0.imprint","IMPRINT",EDGE,{"disambiguationData":[TD([[makeQuery(id+"F0.imprint","INTERSECT",VERTEX,{"derivedFrom":[sQuery(id+"F0.wireOp",EDGE,"E21"),subQ0]}),-1.0]])],"derivedFrom":subQ0})])],"isStart":false});}
            var Q1;
            {var subQ0=sQuery(id+"F0.wireOp",EDGE,"E5");Q1=makeQuery(id+"F3.opExtrude","CAP_EDGE",EDGE,{"disambiguationData":[OSD([subQ0]),TDD([makeQuery(id+"F0.imprint","IMPRINT",EDGE,{"disambiguationData":[TD([[makeQuery(id+"F0.imprint","INTERSECT",VERTEX,{"disambiguationData":[OD(1.0)],"derivedFrom":[subQ0,sQuery(id+"F0.wireOp",EDGE,"E28")]}),-1.0]])],"derivedFrom":subQ0})])],"isStart":false});}
            var Q2;
            Q2=makeQuery(id+"F3.opExtrude","CAP_EDGE",EDGE,{"disambiguationData":[OSD([sQuery(id+"F0.wireOp",EDGE,"E28")])],"isStart":false});
            var Q3;
            {var subQ0=sQuery(id+"F0.wireOp",EDGE,"E5");Q3=makeQuery(id+"F3.opExtrude","CAP_EDGE",EDGE,{"disambiguationData":[OSD([subQ0]),TDD([makeQuery(id+"F0.imprint","IMPRINT",EDGE,{"disambiguationData":[TD([[makeQuery(id+"F0.imprint","INTERSECT",VERTEX,{"disambiguationData":[OD(0.0)],"derivedFrom":[subQ0,sQuery(id+"F0.wireOp",EDGE,"E28")]}),1.0]])],"derivedFrom":subQ0})])],"isStart":false});}
            var Q4;
            Q4=makeQuery(id+"F3.opExtrude","CAP_EDGE",EDGE,{"disambiguationData":[OSD([sQuery(id+"F0.wireOp",EDGE,"E22")])],"isStart":false});
            var Q5;
            {var subQ0=sQuery(id+"F0.wireOp",EDGE,"E23");Q5=makeQuery(id+"F3.opExtrude","CAP_EDGE",EDGE,{"disambiguationData":[OSD([subQ0]),TDD([makeQuery(id+"F0.imprint","IMPRINT",EDGE,{"disambiguationData":[TD([[makeQuery(id+"F0.imprint","INTERSECT",VERTEX,{"derivedFrom":[sQuery(id+"F0.wireOp",EDGE,"E21"),subQ0]}),1.0]])],"derivedFrom":subQ0})])],"isStart":false});}
            var Q6;
            {var subQ0=sQuery(id+"F0.wireOp",EDGE,"E21");Q6=makeQuery(id+"F3.opExtrude","CAP_EDGE",EDGE,{"disambiguationData":[OSD([subQ0]),TDD([makeQuery(id+"F0.imprint","IMPRINT",EDGE,{"disambiguationData":[TD([[makeQuery(id+"F0.imprint","INTERSECT",VERTEX,{"derivedFrom":[subQ0,sQuery(id+"F0.wireOp",EDGE,"E23")]}),1.0]])],"derivedFrom":subQ0})])],"isStart":false});}
            var Q7;
            {var subQ0=sQuery(id+"F0.wireOp",EDGE,"E3");var subQ1=makeQuery(id+"F0.imprint","INTERSECT",VERTEX,{"disambiguationData":[OD(1.0)],"derivedFrom":[subQ0,sQuery(id+"F0.wireOp",EDGE,"E25")]});Q7=makeQuery(id+"F3.opExtrude","CAP_EDGE",EDGE,{"disambiguationData":[OSD([subQ0]),TDD([makeQuery(id+"F0.imprint","IMPRINT",EDGE,{"disambiguationData":[TD([[makeQuery(id+"F0.imprint","INTERSECT",VERTEX,{"disambiguationData":[OD(1.0)],"derivedFrom":[subQ0,sQuery(id+"F0.wireOp",EDGE,"E29")]}),-1.0]])],"derivedFrom":subQ0}),makeQuery(id+"F0.imprint","IMPRINT",EDGE,{"disambiguationData":[TD([[subQ1,-1.0]])],"derivedFrom":subQ0})])],"isStart":false});}
            var Q8;
            {var subQ0=sQuery(id+"F0.wireOp",EDGE,"E3");var subQ1=makeQuery(id+"F0.imprint","INTERSECT",VERTEX,{"disambiguationData":[OD(0.0)],"derivedFrom":[subQ0,sQuery(id+"F0.wireOp",EDGE,"E25")]});Q8=makeQuery(id+"F3.opExtrude","CAP_EDGE",EDGE,{"disambiguationData":[OSD([subQ0]),TDD([makeQuery(id+"F0.imprint","IMPRINT",EDGE,{"disambiguationData":[TD([[makeQuery(id+"F0.imprint","INTERSECT",VERTEX,{"disambiguationData":[OD(0.0)],"derivedFrom":[subQ0,sQuery(id+"F0.wireOp",EDGE,"E21")]}),-1.0]])],"derivedFrom":subQ0}),makeQuery(id+"F0.imprint","IMPRINT",EDGE,{"disambiguationData":[TD([[subQ1,-1.0]])],"derivedFrom":subQ0})])],"isStart":false});}
            var Q9;
            {var subQ0=sQuery(id+"F0.wireOp",EDGE,"E21");Q9=makeQuery(id+"F3.opExtrude","CAP_EDGE",EDGE,{"disambiguationData":[OSD([subQ0]),TDD([makeQuery(id+"F0.imprint","IMPRINT",EDGE,{"disambiguationData":[TD([[makeQuery(id+"F0.imprint","INTERSECT",VERTEX,{"derivedFrom":[subQ0,sQuery(id+"F0.wireOp",EDGE,"E24")]}),-1.0]])],"derivedFrom":subQ0})])],"isStart":false});}
            var Q10;
            Q10=makeQuery(id+"F3.opExtrude","CAP_EDGE",EDGE,{"disambiguationData":[OSD([sQuery(id+"F0.wireOp",EDGE,"E27")])],"isStart":false});
            var Q11;
            {var subQ0=sQuery(id+"F0.wireOp",EDGE,"E4");Q11=makeQuery(id+"F3.opExtrude","CAP_EDGE",EDGE,{"disambiguationData":[OSD([subQ0]),TDD([makeQuery(id+"F0.imprint","IMPRINT",EDGE,{"disambiguationData":[TD([[makeQuery(id+"F0.imprint","INTERSECT",VERTEX,{"disambiguationData":[OD(0.0)],"derivedFrom":[subQ0,sQuery(id+"F0.wireOp",EDGE,"E23")]}),-1.0]])],"derivedFrom":subQ0})])],"isStart":false});}
            var Q12;
            {var subQ0=sQuery(id+"F0.wireOp",EDGE,"E4");Q12=makeQuery(id+"F3.opExtrude","CAP_EDGE",EDGE,{"disambiguationData":[OSD([subQ0]),TDD([makeQuery(id+"F0.imprint","IMPRINT",EDGE,{"disambiguationData":[TD([[makeQuery(id+"F0.imprint","INTERSECT",VERTEX,{"disambiguationData":[OD(1.0)],"derivedFrom":[subQ0,sQuery(id+"F0.wireOp",EDGE,"E27")]}),-1.0]])],"derivedFrom":subQ0})])],"isStart":false});}
            fillet(context, id + "F5", {"entities" : qUnion([Q0, Q1, Q2, Q3, Q4, Q5, Q6, Q7, Q8, Q9, Q10, Q11, Q12]), "radius" : 2 * mm, "tangentPropagation" : true, "allowEdgeOverflow" : false});
        }
        {
            var Q0;
            {var subQ0=sQuery(id+"F0.wireOp",EDGE,"E31");var subQ1=sQuery(id+"F0.wireOp",EDGE,"E9");var subQ2=makeQuery(id+"F0.imprint","INTERSECT",VERTEX,{"disambiguationData":[OD(0.0)],"derivedFrom":[subQ1,subQ0]});Q0=makeQuery(id+"F0.imprint","IMPRINT",FACE,{"disambiguationData":[TD([[makeQuery(id+"F0.imprint","IMPRINT",EDGE,{"disambiguationData":[TD([[subQ2,-1.0]])],"derivedFrom":subQ1}),-1.0]])]});}
            var Q1;
            {var subQ0=sQuery(id+"F0.wireOp",EDGE,"E31");var subQ1=sQuery(id+"F0.wireOp",EDGE,"E10");var subQ2=makeQuery(id+"F0.imprint","INTERSECT",VERTEX,{"disambiguationData":[OD(0.0)],"derivedFrom":[subQ1,subQ0]});Q1=makeQuery(id+"F0.imprint","IMPRINT",FACE,{"disambiguationData":[TD([[makeQuery(id+"F0.imprint","IMPRINT",EDGE,{"disambiguationData":[TD([[subQ2,-1.0]])],"derivedFrom":subQ1}),-1.0]])]});}
            var Q2;
            {var subQ4=sQuery(id+"F0.wireOp",EDGE,"E31");var subQ7=sQuery(id+"F0.wireOp",EDGE,"E22");var subQ9=makeQuery(id+"F0.imprint","INTERSECT",VERTEX,{"disambiguationData":[OD(0.0)],"derivedFrom":[subQ7,subQ4]});Q2=makeQuery(id+"F0.imprint","IMPRINT",FACE,{"disambiguationData":[TD([[makeQuery(id+"F0.imprint","IMPRINT",EDGE,{"disambiguationData":[TD([[subQ9,-1.0]])],"derivedFrom":subQ7}),1.0]])]});}
            var Q3;
            {var subQ0=sQuery(id+"F0.wireOp",EDGE,"E29");var subQ1=sQuery(id+"F0.wireOp",EDGE,"E10");var subQ2=makeQuery(id+"F0.imprint","INTERSECT",VERTEX,{"disambiguationData":[OD(1.0)],"derivedFrom":[subQ1,subQ0]});Q3=makeQuery(id+"F0.imprint","IMPRINT",FACE,{"disambiguationData":[TD([[makeQuery(id+"F0.imprint","IMPRINT",EDGE,{"disambiguationData":[TD([[subQ2,-1.0]])],"derivedFrom":subQ1}),-1.0]])]});}
            var Q4;
            {var subQ0=sQuery(id+"F0.wireOp",EDGE,"E29");var subQ1=sQuery(id+"F0.wireOp",EDGE,"E9");var subQ2=makeQuery(id+"F0.imprint","INTERSECT",VERTEX,{"disambiguationData":[OD(1.0)],"derivedFrom":[subQ1,subQ0]});Q4=makeQuery(id+"F0.imprint","IMPRINT",FACE,{"disambiguationData":[TD([[makeQuery(id+"F0.imprint","IMPRINT",EDGE,{"disambiguationData":[TD([[subQ2,-1.0]])],"derivedFrom":subQ1}),-1.0]])]});}
            var Q5;
            {var subQ1=sQuery(id+"F0.wireOp",EDGE,"E3");var subQ5=sQuery(id+"F0.wireOp",EDGE,"E29");var subQ6=makeQuery(id+"F0.imprint","INTERSECT",VERTEX,{"disambiguationData":[OD(1.0)],"derivedFrom":[subQ1,subQ5]});Q5=makeQuery(id+"F0.imprint","IMPRINT",FACE,{"disambiguationData":[TD([[makeQuery(id+"F0.imprint","IMPRINT",EDGE,{"disambiguationData":[TD([[subQ6,-1.0]])],"derivedFrom":subQ1}),-1.0]])]});}
            var Q6;
            {var subQ1=sQuery(id+"F0.wireOp",EDGE,"E3");var subQ7=sQuery(id+"F0.wireOp",EDGE,"E25");var subQ8=makeQuery(id+"F0.imprint","INTERSECT",VERTEX,{"disambiguationData":[OD(0.0)],"derivedFrom":[subQ1,subQ7]});Q6=makeQuery(id+"F0.imprint","IMPRINT",FACE,{"disambiguationData":[TD([[makeQuery(id+"F0.imprint","IMPRINT",EDGE,{"disambiguationData":[TD([[subQ8,-1.0]])],"derivedFrom":subQ1}),-1.0]])]});}
            extrude(context, id + "F6", {"entities" : qUnion([Q0, Q1, Q2, Q3, Q4, Q5, Q6]), "depth" : 14 * mm});
        }
        {
            var Q0;
            {var subQ0=sQuery(id+"F0.wireOp",EDGE,"E31");var subQ1=makeQuery(id+"F0.imprint","INTERSECT",VERTEX,{"disambiguationData":[OD(1.0)],"derivedFrom":[sQuery(id+"F0.wireOp",EDGE,"E9"),subQ0]});var subQ2=makeQuery(id+"F0.imprint","INTERSECT",VERTEX,{"disambiguationData":[OD(1.0)],"derivedFrom":[sQuery(id+"F0.wireOp",EDGE,"E10"),subQ0]});Q0=makeQuery(id+"F6.opExtrude","CAP_EDGE",EDGE,{"disambiguationData":[OSD([subQ0]),TDD([makeQuery(id+"F0.imprint","IMPRINT",EDGE,{"disambiguationData":[TD([[subQ1,-1.0]])],"derivedFrom":subQ0}),makeQuery(id+"F0.imprint","IMPRINT",EDGE,{"disambiguationData":[TD([[makeQuery(id+"F0.imprint","INTERSECT",VERTEX,{"disambiguationData":[OD(1.0)],"derivedFrom":[sQuery(id+"F0.wireOp",EDGE,"E22"),subQ0]}),-1.0]])],"derivedFrom":subQ0}),makeQuery(id+"F0.imprint","IMPRINT",EDGE,{"disambiguationData":[TD([[subQ2,1.0]])],"derivedFrom":subQ0}),makeQuery(id+"F0.imprint","IMPRINT",EDGE,{"disambiguationData":[TD([[subQ1,1.0]])],"derivedFrom":subQ0})])],"isStart":false});}
            fillet(context, id + "F7", {"entities" : qUnion([Q0]), "radius" : 4 * mm, "tangentPropagation" : true, "allowEdgeOverflow" : false});
        }
        {
            var Q0;
            {var subQ0=sQuery(id+"F0.wireOp",EDGE,"E30");Q0=makeQuery(id+"F2.opExtrude","CAP_EDGE",EDGE,{"disambiguationData":[OSD([subQ0]),TDD([makeQuery(id+"F0.imprint","IMPRINT",EDGE,{"derivedFrom":subQ0})])],"isStart":false});}
            fillet(context, id + "F8", {"entities" : qUnion([Q0]), "radius" : 4.8 * mm, "tangentPropagation" : true, "allowEdgeOverflow" : false});
        }
        {
            var Q0;
            Q0=qCreatedBy(makeId("Front.planeOp"),FACE);
            var sketch = newSketch(context, id + "F9", { "sketchPlane" : qUnion([Q0])});
            skCircle(sketch, "E32", {"center": v(15.8, 38.44) * mm, "radius": 0.5 * mm});
            skSolve(sketch);
        }
        {
            var Q0;
            Q0=sQuery(id+"F9.wireOp",EDGE,"E32");
            var Q1;
            Q1=sQuery(id+"F0.wireOp",EDGE,"E29");
            revolve(context, id + "F10", {"bodyType" : ToolBodyType.SURFACE, "surfaceEntities" : qUnion([Q0]), "axis" : qUnion([Q1]), "revolveType" : RevolveType.FULL});
        }
    });
